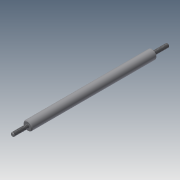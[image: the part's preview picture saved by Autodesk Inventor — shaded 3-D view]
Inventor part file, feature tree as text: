
AUTODESK INVENTOR PART (.ipt)
format: ipt  version: 2015 (Build 190159000, 159)  size: 110,592 bytes
history: native  units: mm
features: sketch x5, extrude x3, chamfer x3, hole x2, thread x2
ambient origin geometry x8: Origin, YZ Plane, XZ Plane, XY Plane, X Axis, Y Axis, Z Axis, Center Point
bodies: Solid1 (feature_tree)
feature tree (15):
  extrude  "Extrusion1"  Depth=82.6mm TaperAngle=0.0deg
  hole  "Hole1"  [1 undecoded]
  hole  "Hole2"  [1 undecoded]
  chamfer  "Chamfer1"  Distance=10.0mm
  extrude  "Extrusion2"  Depth=10.0mm TaperAngle=45.0deg
  extrude  "Extrusion3"  Depth=10.0mm TaperAngle=45.0deg
  thread  "Thread1"  [1 undecoded]
  thread  "Thread2"  [1 undecoded]
  chamfer  "Chamfer2"  [1 undecoded]
  chamfer  "Chamfer3"  [1 undecoded]
  sketch  "Sketch1"  dims[d0=6.0mm d1=82.6mm d2=0.0mm]
  sketch  "Sketch2"  dims[d3=2.459mm d4=6.0mm d5=4.0mm d6=2.0mm d7=90.0deg d8=8.0mm d9=0.0mm]
  sketch  "Sketch3"  dims[d10=2.459mm d11=6.0mm d12=4.0mm d13=2.0mm d14=90.0deg d15=8.0mm d16=0.0mm d17=0.5mm d18=2.0mm d19=45.0deg]
  sketch  "Sketch4"  dims[d20=10.0mm d21=0.0mm d22=10.0mm d23=0.0mm d24=10.0mm d25=0.0mm]
  sketch  "Sketch5"  dims[d26=10.0mm d27=0.0mm d28=0.3mm d29=2.0mm d30=45.0deg d31=0.3mm d32=2.0mm d33=45.0deg]
note: 6 required parameter values undecoded (feature->parameter linkage not recoverable at this tier; creation-order binding heuristic only, values carry confidence <= 0.55)
